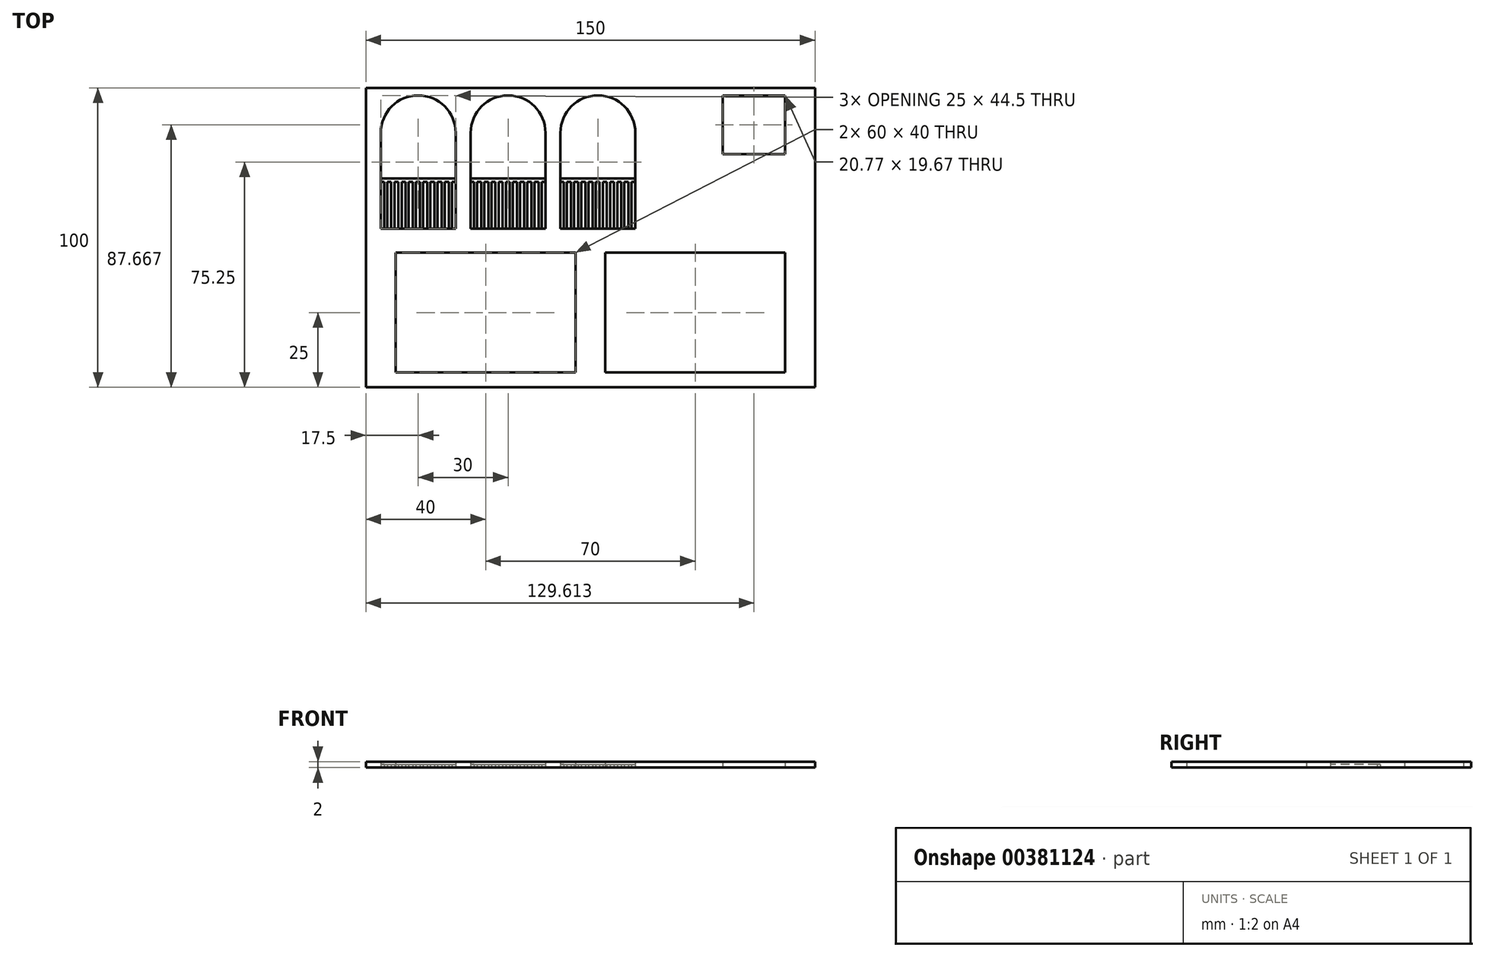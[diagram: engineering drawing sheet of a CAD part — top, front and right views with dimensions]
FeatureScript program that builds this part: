
annotation { "Feature Type Name" : "Feature", "Feature Type Description" : "" }
export const myFeature = defineFeature(function(context is Context, id is Id, definition is map)
    precondition{}
    {
        {
            var Q0;
            Q0=qCreatedBy(makeId("Top.planeOp"),FACE);
            var sketch = newSketch(context, id + "F0", { "sketchPlane" : qUnion([Q0])});
            skLineSegment(sketch, "E0.bottom", {"start": v(75, 50) * mm, "end": v(-75, 50) * mm});
            skLineSegment(sketch, "E0.top", {"start": v(75, -50) * mm, "end": v(-75, -50) * mm});
            skLineSegment(sketch, "E0.left", {"start": v(75, 50) * mm, "end": v(75, -50) * mm});
            skLineSegment(sketch, "E0.right", {"start": v(-75, 50) * mm, "end": v(-75, -50) * mm});
            skPoint(sketch, "E0.middle", {"position": v(0, 0) * mm});
            skLineSegment(sketch, "E1.bottom", {"start": v(-5, -45) * mm, "end": v(-65, -45) * mm});
            skLineSegment(sketch, "E1.top", {"start": v(-5, -5) * mm, "end": v(-65, -5) * mm});
            skLineSegment(sketch, "E1.left", {"start": v(-5, -45) * mm, "end": v(-5, -5) * mm});
            skLineSegment(sketch, "E1.right", {"start": v(-65, -45) * mm, "end": v(-65, -5) * mm});
            skPoint(sketch, "E1.middle", {"position": v(-35, -25) * mm});
            skLineSegment(sketch, "E2.bottom", {"start": v(65, -45) * mm, "end": v(5, -45) * mm});
            skLineSegment(sketch, "E2.top", {"start": v(65, -5) * mm, "end": v(5, -5) * mm});
            skLineSegment(sketch, "E2.left", {"start": v(65, -45) * mm, "end": v(65, -5) * mm});
            skLineSegment(sketch, "E2.right", {"start": v(5, -45) * mm, "end": v(5, -5) * mm});
            skPoint(sketch, "E2.middle", {"position": v(35, -25) * mm});
            skLineSegment(sketch, "E3.bottom", {"start": v(65, 27.83) * mm, "end": v(44.23, 27.83) * mm});
            skLineSegment(sketch, "E3.top", {"start": v(65, 47.5) * mm, "end": v(44.23, 47.5) * mm});
            skLineSegment(sketch, "E3.left", {"start": v(65, 27.83) * mm, "end": v(65, 47.5) * mm});
            skLineSegment(sketch, "E3.right", {"start": v(44.23, 27.83) * mm, "end": v(44.23, 47.5) * mm});
            skPoint(sketch, "E3.middle", {"position": v(54.61, 37.67) * mm});
            skArc(sketch, "E4", {"start": v(-45, 35) * mm, "mid": v(-57.5, 47.5) * mm, "end": v(-70, 35) * mm});
            skLineSegment(sketch, "E5", {"start": v(-70, 35) * mm, "end": v(-70, 3) * mm});
            skLineSegment(sketch, "E6", {"start": v(-45, 35) * mm, "end": v(-45, 3) * mm});
            skLineSegment(sketch, "E7.left", {"start": v(-68.9, 18.66) * mm, "end": v(-68.9, 3) * mm});
            skLineSegment(sketch, "E7.right", {"start": v(-67.85, 18.66) * mm, "end": v(-67.85, 3) * mm});
            skLineSegment(sketch, "E8.1.0.0", {"start": v(-65.45, 18.66) * mm, "end": v(-65.45, 3) * mm});
            skLineSegment(sketch, "E8.1.0.1", {"start": v(-66.5, 18.66) * mm, "end": v(-66.5, 3) * mm});
            skLineSegment(sketch, "E8.2.0.0", {"start": v(-63.05, 18.66) * mm, "end": v(-63.05, 3) * mm});
            skLineSegment(sketch, "E8.2.0.1", {"start": v(-64.1, 18.66) * mm, "end": v(-64.1, 3) * mm});
            skLineSegment(sketch, "E8.3.0.0", {"start": v(-60.65, 18.66) * mm, "end": v(-60.65, 3) * mm});
            skLineSegment(sketch, "E8.3.0.1", {"start": v(-61.7, 18.66) * mm, "end": v(-61.7, 3) * mm});
            skLineSegment(sketch, "E8.4.0.0", {"start": v(-58.25, 18.66) * mm, "end": v(-58.25, 3) * mm});
            skLineSegment(sketch, "E8.4.0.1", {"start": v(-59.3, 18.66) * mm, "end": v(-59.3, 3) * mm});
            skLineSegment(sketch, "E8.5.0.0", {"start": v(-55.85, 18.66) * mm, "end": v(-55.85, 3) * mm});
            skLineSegment(sketch, "E8.5.0.1", {"start": v(-56.9, 18.66) * mm, "end": v(-56.9, 3) * mm});
            skLineSegment(sketch, "E8.6.0.0", {"start": v(-53.45, 18.66) * mm, "end": v(-53.45, 3) * mm});
            skLineSegment(sketch, "E8.6.0.1", {"start": v(-54.5, 18.66) * mm, "end": v(-54.5, 3) * mm});
            skLineSegment(sketch, "E8.7.0.0", {"start": v(-51.05, 18.66) * mm, "end": v(-51.05, 3) * mm});
            skLineSegment(sketch, "E8.7.0.1", {"start": v(-52.1, 18.66) * mm, "end": v(-52.1, 3) * mm});
            skLineSegment(sketch, "E8.8.0.0", {"start": v(-48.65, 18.66) * mm, "end": v(-48.65, 3) * mm});
            skLineSegment(sketch, "E8.8.0.1", {"start": v(-49.7, 18.66) * mm, "end": v(-49.7, 3) * mm});
            skLineSegment(sketch, "E8.9.0.0", {"start": v(-46.25, 18.66) * mm, "end": v(-46.25, 3) * mm});
            skLineSegment(sketch, "E8.9.0.1", {"start": v(-47.3, 18.66) * mm, "end": v(-47.3, 3) * mm});
            skLineSegment(sketch, "E9.top", {"start": v(-70, 19.71) * mm, "end": v(-45, 19.71) * mm});
            skLineSegment(sketch, "E9.left", {"start": v(-70, 18.66) * mm, "end": v(-70, 19.71) * mm});
            skLineSegment(sketch, "E9.right", {"start": v(-45, 18.66) * mm, "end": v(-45, 19.71) * mm});
            skLineSegment(sketch, "E10", {"start": v(-67.85, 18.66) * mm, "end": v(-66.5, 18.66) * mm});
            skLineSegment(sketch, "E11", {"start": v(-68.9, 18.66) * mm, "end": v(-70, 18.66) * mm});
            skLineSegment(sketch, "E12", {"start": v(-65.45, 18.66) * mm, "end": v(-64.1, 18.66) * mm});
            skLineSegment(sketch, "E13", {"start": v(-63.05, 18.66) * mm, "end": v(-61.7, 18.66) * mm});
            skLineSegment(sketch, "E14", {"start": v(-60.65, 18.66) * mm, "end": v(-59.3, 18.66) * mm});
            skLineSegment(sketch, "E15", {"start": v(-58.25, 18.66) * mm, "end": v(-56.9, 18.66) * mm});
            skLineSegment(sketch, "E16", {"start": v(-55.85, 18.66) * mm, "end": v(-54.5, 18.66) * mm});
            skLineSegment(sketch, "E17", {"start": v(-53.45, 18.66) * mm, "end": v(-52.1, 18.66) * mm});
            skLineSegment(sketch, "E18", {"start": v(-51.05, 18.66) * mm, "end": v(-49.7, 18.66) * mm});
            skLineSegment(sketch, "E19", {"start": v(-48.65, 18.66) * mm, "end": v(-47.3, 18.66) * mm});
            skLineSegment(sketch, "E20", {"start": v(-46.25, 18.66) * mm, "end": v(-45, 18.66) * mm});
            skLineSegment(sketch, "E21.1.0.0", {"start": v(-30.65, 18.66) * mm, "end": v(-30.65, 3) * mm});
            skLineSegment(sketch, "E21.1.0.1", {"start": v(-29.3, 18.66) * mm, "end": v(-29.3, 3) * mm});
            skLineSegment(sketch, "E21.1.0.2", {"start": v(-24.5, 18.66) * mm, "end": v(-24.5, 3) * mm});
            skLineSegment(sketch, "E21.1.0.3", {"start": v(-19.7, 18.66) * mm, "end": v(-19.7, 3) * mm});
            skLineSegment(sketch, "E21.1.0.4", {"start": v(-22.1, 18.66) * mm, "end": v(-22.1, 3) * mm});
            skLineSegment(sketch, "E21.1.0.5", {"start": v(-23.45, 18.66) * mm, "end": v(-23.45, 3) * mm});
            skLineSegment(sketch, "E21.1.0.6", {"start": v(-18.65, 18.66) * mm, "end": v(-18.65, 3) * mm});
            skLineSegment(sketch, "E21.1.0.7", {"start": v(-37.85, 18.66) * mm, "end": v(-37.85, 3) * mm});
            skLineSegment(sketch, "E21.1.0.8", {"start": v(-21.05, 18.66) * mm, "end": v(-21.05, 3) * mm});
            skLineSegment(sketch, "E21.1.0.9", {"start": v(-40, 35) * mm, "end": v(-40, 3) * mm});
            skLineSegment(sketch, "E21.1.0.10", {"start": v(-17.3, 18.66) * mm, "end": v(-17.3, 3) * mm});
            skLineSegment(sketch, "E21.1.0.11", {"start": v(-36.5, 18.66) * mm, "end": v(-36.5, 3) * mm});
            skLineSegment(sketch, "E21.1.0.12", {"start": v(-38.9, 18.66) * mm, "end": v(-38.9, 3) * mm});
            skLineSegment(sketch, "E21.1.0.13", {"start": v(-35.45, 18.66) * mm, "end": v(-35.45, 3) * mm});
            skLineSegment(sketch, "E21.1.0.14", {"start": v(-26.9, 18.66) * mm, "end": v(-26.9, 3) * mm});
            skLineSegment(sketch, "E21.1.0.15", {"start": v(-15, 35) * mm, "end": v(-15, 3) * mm});
            skLineSegment(sketch, "E21.1.0.16", {"start": v(-16.25, 18.66) * mm, "end": v(-16.25, 3) * mm});
            skLineSegment(sketch, "E21.1.0.17", {"start": v(-28.25, 18.66) * mm, "end": v(-28.25, 3) * mm});
            skLineSegment(sketch, "E21.1.0.18", {"start": v(-25.85, 18.66) * mm, "end": v(-25.85, 3) * mm});
            skArc(sketch, "E21.1.0.19", {"start": v(-15, 35) * mm, "mid": v(-27.5, 47.5) * mm, "end": v(-40, 35) * mm});
            skLineSegment(sketch, "E21.1.0.20", {"start": v(-34.1, 18.66) * mm, "end": v(-34.1, 3) * mm});
            skLineSegment(sketch, "E21.1.0.21", {"start": v(-31.7, 18.66) * mm, "end": v(-31.7, 3) * mm});
            skLineSegment(sketch, "E21.1.0.22", {"start": v(-33.05, 18.66) * mm, "end": v(-33.05, 3) * mm});
            skLineSegment(sketch, "E21.1.0.23", {"start": v(-28.25, 18.66) * mm, "end": v(-26.9, 18.66) * mm});
            skLineSegment(sketch, "E21.1.0.26", {"start": v(-15, 18.66) * mm, "end": v(-15, 19.71) * mm});
            skLineSegment(sketch, "E21.1.0.27", {"start": v(-33.05, 18.66) * mm, "end": v(-31.7, 18.66) * mm});
            skLineSegment(sketch, "E21.1.0.28", {"start": v(-35.45, 18.66) * mm, "end": v(-34.1, 18.66) * mm});
            skLineSegment(sketch, "E21.1.0.30", {"start": v(-40, 19.71) * mm, "end": v(-15, 19.71) * mm});
            skLineSegment(sketch, "E21.1.0.31", {"start": v(-40, 18.66) * mm, "end": v(-40, 19.71) * mm});
            skLineSegment(sketch, "E21.1.0.33", {"start": v(-21.05, 18.66) * mm, "end": v(-19.7, 18.66) * mm});
            skLineSegment(sketch, "E21.1.0.37", {"start": v(-30.65, 18.66) * mm, "end": v(-29.3, 18.66) * mm});
            skLineSegment(sketch, "E21.1.0.38", {"start": v(-23.45, 18.66) * mm, "end": v(-22.1, 18.66) * mm});
            skLineSegment(sketch, "E21.1.0.41", {"start": v(-38.9, 18.66) * mm, "end": v(-40, 18.66) * mm});
            skLineSegment(sketch, "E21.1.0.42", {"start": v(-18.65, 18.66) * mm, "end": v(-17.3, 18.66) * mm});
            skLineSegment(sketch, "E21.1.0.43", {"start": v(-16.25, 18.66) * mm, "end": v(-15, 18.66) * mm});
            skLineSegment(sketch, "E21.1.0.44", {"start": v(-25.85, 18.66) * mm, "end": v(-24.5, 18.66) * mm});
            skLineSegment(sketch, "E21.1.0.45", {"start": v(-37.85, 18.66) * mm, "end": v(-36.5, 18.66) * mm});
            skLineSegment(sketch, "E21.2.0.0", {"start": v(-0.65, 18.66) * mm, "end": v(-0.65, 3) * mm});
            skLineSegment(sketch, "E21.2.0.1", {"start": v(0.7, 18.66) * mm, "end": v(0.7, 3) * mm});
            skLineSegment(sketch, "E21.2.0.2", {"start": v(5.5, 18.66) * mm, "end": v(5.5, 3) * mm});
            skLineSegment(sketch, "E21.2.0.3", {"start": v(10.3, 18.66) * mm, "end": v(10.3, 3) * mm});
            skLineSegment(sketch, "E21.2.0.4", {"start": v(7.9, 18.66) * mm, "end": v(7.9, 3) * mm});
            skLineSegment(sketch, "E21.2.0.5", {"start": v(6.55, 18.66) * mm, "end": v(6.55, 3) * mm});
            skLineSegment(sketch, "E21.2.0.6", {"start": v(11.35, 18.66) * mm, "end": v(11.35, 3) * mm});
            skLineSegment(sketch, "E21.2.0.7", {"start": v(-7.85, 18.66) * mm, "end": v(-7.85, 3) * mm});
            skLineSegment(sketch, "E21.2.0.8", {"start": v(8.95, 18.66) * mm, "end": v(8.95, 3) * mm});
            skLineSegment(sketch, "E21.2.0.9", {"start": v(-10, 35) * mm, "end": v(-10, 3) * mm});
            skLineSegment(sketch, "E21.2.0.10", {"start": v(12.7, 18.66) * mm, "end": v(12.7, 3) * mm});
            skLineSegment(sketch, "E21.2.0.11", {"start": v(-6.5, 18.66) * mm, "end": v(-6.5, 3) * mm});
            skLineSegment(sketch, "E21.2.0.12", {"start": v(-8.9, 18.66) * mm, "end": v(-8.9, 3) * mm});
            skLineSegment(sketch, "E21.2.0.13", {"start": v(-5.45, 18.66) * mm, "end": v(-5.45, 3) * mm});
            skLineSegment(sketch, "E21.2.0.14", {"start": v(3.1, 18.66) * mm, "end": v(3.1, 3) * mm});
            skLineSegment(sketch, "E21.2.0.15", {"start": v(15, 35) * mm, "end": v(15, 3) * mm});
            skLineSegment(sketch, "E21.2.0.16", {"start": v(13.75, 18.66) * mm, "end": v(13.75, 3) * mm});
            skLineSegment(sketch, "E21.2.0.17", {"start": v(1.75, 18.66) * mm, "end": v(1.75, 3) * mm});
            skLineSegment(sketch, "E21.2.0.18", {"start": v(4.15, 18.66) * mm, "end": v(4.15, 3) * mm});
            skArc(sketch, "E21.2.0.19", {"start": v(15, 35) * mm, "mid": v(2.5, 47.5) * mm, "end": v(-10, 35) * mm});
            skLineSegment(sketch, "E21.2.0.20", {"start": v(-4.1, 18.66) * mm, "end": v(-4.1, 3) * mm});
            skLineSegment(sketch, "E21.2.0.21", {"start": v(-1.7, 18.66) * mm, "end": v(-1.7, 3) * mm});
            skLineSegment(sketch, "E21.2.0.22", {"start": v(-3.05, 18.66) * mm, "end": v(-3.05, 3) * mm});
            skLineSegment(sketch, "E21.2.0.23", {"start": v(1.75, 18.66) * mm, "end": v(3.1, 18.66) * mm});
            skLineSegment(sketch, "E21.2.0.26", {"start": v(15, 18.66) * mm, "end": v(15, 19.71) * mm});
            skLineSegment(sketch, "E21.2.0.27", {"start": v(-3.05, 18.66) * mm, "end": v(-1.7, 18.66) * mm});
            skLineSegment(sketch, "E21.2.0.28", {"start": v(-5.45, 18.66) * mm, "end": v(-4.1, 18.66) * mm});
            skLineSegment(sketch, "E21.2.0.30", {"start": v(-10, 19.71) * mm, "end": v(15, 19.71) * mm});
            skLineSegment(sketch, "E21.2.0.31", {"start": v(-10, 18.66) * mm, "end": v(-10, 19.71) * mm});
            skLineSegment(sketch, "E21.2.0.33", {"start": v(8.95, 18.66) * mm, "end": v(10.3, 18.66) * mm});
            skLineSegment(sketch, "E21.2.0.37", {"start": v(-0.65, 18.66) * mm, "end": v(0.7, 18.66) * mm});
            skLineSegment(sketch, "E21.2.0.38", {"start": v(6.55, 18.66) * mm, "end": v(7.9, 18.66) * mm});
            skLineSegment(sketch, "E21.2.0.41", {"start": v(-8.9, 18.66) * mm, "end": v(-10, 18.66) * mm});
            skLineSegment(sketch, "E21.2.0.42", {"start": v(11.35, 18.66) * mm, "end": v(12.7, 18.66) * mm});
            skLineSegment(sketch, "E21.2.0.43", {"start": v(13.75, 18.66) * mm, "end": v(15, 18.66) * mm});
            skLineSegment(sketch, "E21.2.0.44", {"start": v(4.15, 18.66) * mm, "end": v(5.5, 18.66) * mm});
            skLineSegment(sketch, "E21.2.0.45", {"start": v(-7.85, 18.66) * mm, "end": v(-6.5, 18.66) * mm});
            skLineSegment(sketch, "E22", {"start": v(-70, 3) * mm, "end": v(-45, 3) * mm});
            skLineSegment(sketch, "E23", {"start": v(-40, 3) * mm, "end": v(-15, 3) * mm});
            skLineSegment(sketch, "E24", {"start": v(-10, 3) * mm, "end": v(15, 3) * mm});
            skSolve(sketch);
        }
        {
            var Q0;
            {var subQ16=sQuery(id+"F0.wireOp",EDGE,"E21.1.0.0");Q0=makeQuery(id+"F0.imprint","IMPRINT",FACE,{"disambiguationData":[TD([[makeQuery(id+"F0.imprint","IMPRINT",EDGE,{"derivedFrom":subQ16}),-1.0]])]});}
            var Q1;
            {var subQ16=sQuery(id+"F0.wireOp",EDGE,"E21.2.0.0");Q1=makeQuery(id+"F0.imprint","IMPRINT",FACE,{"disambiguationData":[TD([[makeQuery(id+"F0.imprint","IMPRINT",EDGE,{"derivedFrom":subQ16}),-1.0]])]});}
            var Q2;
            {var subQ4=sQuery(id+"F0.wireOp",EDGE,"E7.left");Q2=makeQuery(id+"F0.imprint","IMPRINT",FACE,{"disambiguationData":[TD([[makeQuery(id+"F0.imprint","IMPRINT",EDGE,{"derivedFrom":subQ4}),1.0]])]});}
            extrude(context, id + "F1", {"entities" : qUnion([Q0, Q1, Q2]), "depth" : 1 * mm});
        }
        {
            var Q0;
            Q0=makeQuery(id+"F0.imprint","IMPRINT",FACE,{"disambiguationData":[TD([[makeQuery(id+"F0.imprint","IMPRINT",EDGE,{"derivedFrom":sQuery(id+"F0.wireOp",EDGE,"E0.bottom")}),1.0]])]});
            extrude(context, id + "F2", {"entities" : qUnion([Q0]), "depth" : 2 * mm});
        }
    });
